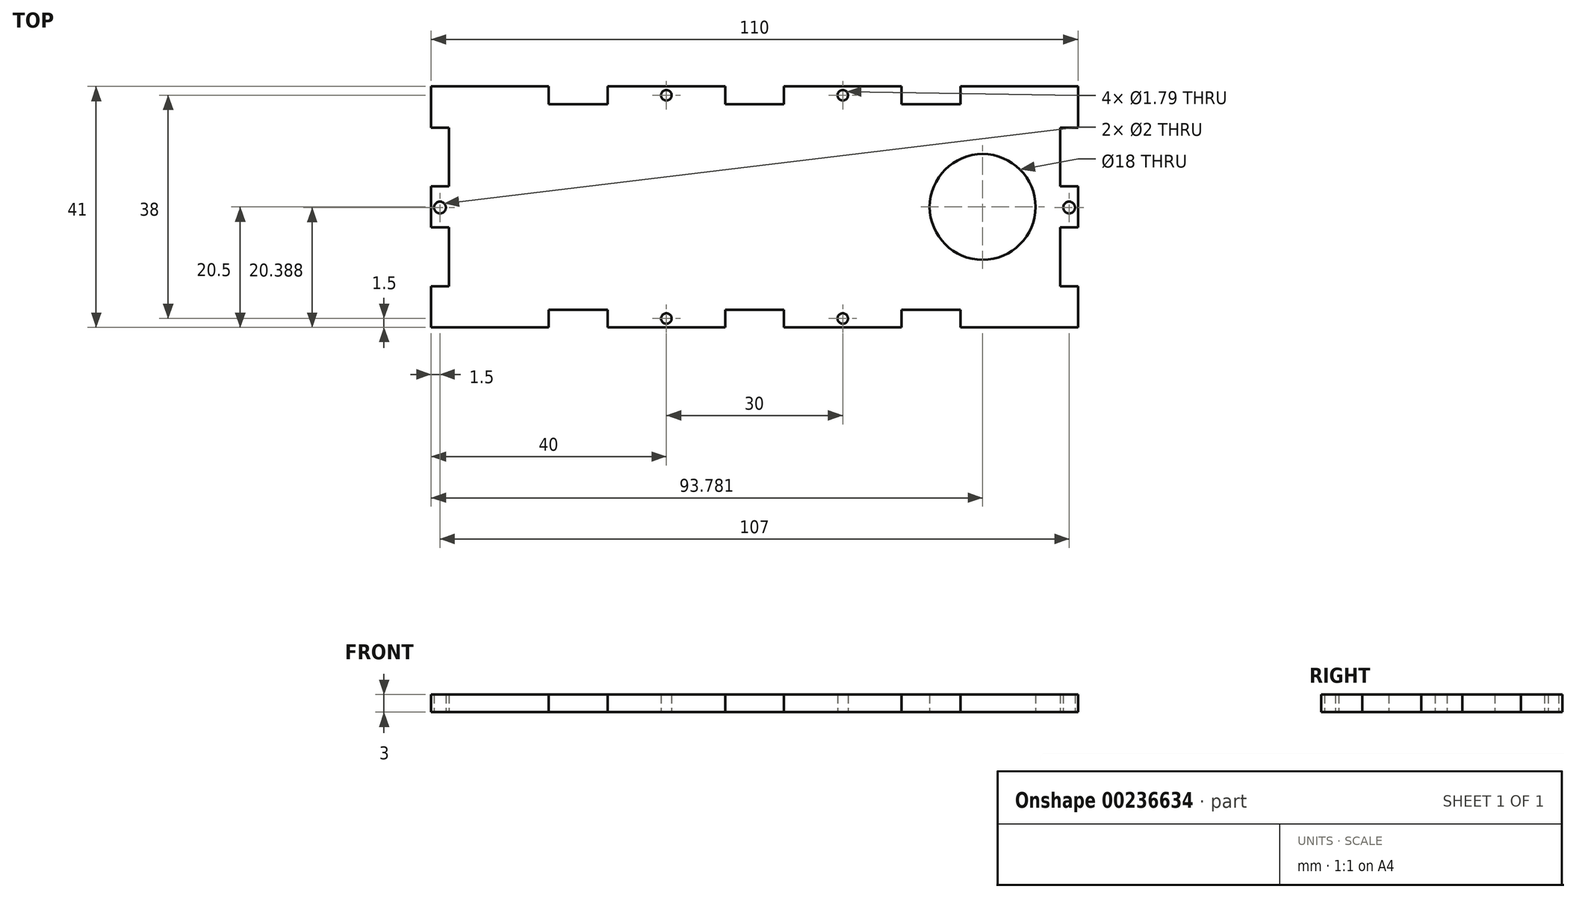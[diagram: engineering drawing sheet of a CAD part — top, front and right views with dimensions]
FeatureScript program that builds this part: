
annotation { "Feature Type Name" : "Feature", "Feature Type Description" : "" }
export const myFeature = defineFeature(function(context is Context, id is Id, definition is map)
    precondition{}
    {
        {
            var Q0;
            Q0=qCreatedBy(makeId("Top.planeOp"),FACE);
            var sketch = newSketch(context, id + "F0", { "sketchPlane" : qUnion([Q0])});
            skLineSegment(sketch, "E0", {"start": v(0, 0) * mm, "end": v(0, 7) * mm});
            skLineSegment(sketch, "E1", {"start": v(0, 7) * mm, "end": v(3, 7) * mm});
            skLineSegment(sketch, "E2", {"start": v(3, 7) * mm, "end": v(3, 17) * mm});
            skLineSegment(sketch, "E3", {"start": v(3, 17) * mm, "end": v(0, 17) * mm});
            skLineSegment(sketch, "E4", {"start": v(0, 17) * mm, "end": v(0, 24) * mm});
            skLineSegment(sketch, "E5", {"start": v(0, 24) * mm, "end": v(3, 24) * mm});
            skLineSegment(sketch, "E6", {"start": v(3, 24) * mm, "end": v(3, 34) * mm});
            skLineSegment(sketch, "E7", {"start": v(3, 34) * mm, "end": v(0, 34) * mm});
            skLineSegment(sketch, "E8", {"start": v(0, 34) * mm, "end": v(0, 41) * mm});
            skLineSegment(sketch, "E9", {"start": v(0, 41) * mm, "end": v(20, 41) * mm});
            skLineSegment(sketch, "E10", {"start": v(20, 41) * mm, "end": v(20, 38) * mm});
            skLineSegment(sketch, "E11", {"start": v(20, 38) * mm, "end": v(30, 38) * mm});
            skLineSegment(sketch, "E12", {"start": v(30, 38) * mm, "end": v(30, 41) * mm});
            skLineSegment(sketch, "E13", {"start": v(30, 41) * mm, "end": v(50, 41) * mm});
            skLineSegment(sketch, "E14", {"start": v(50, 41) * mm, "end": v(50, 38) * mm});
            skLineSegment(sketch, "E15", {"start": v(50, 38) * mm, "end": v(55, 38) * mm});
            skLineSegment(sketch, "E16", {"start": v(55, 41) * mm, "end": v(55, 0) * mm, "construction": true});
            skLineSegment(sketch, "E17", {"start": v(0, 20.5) * mm, "end": v(55, 20.5) * mm, "construction": true});
            skLineSegment(sketch, "E18.MirrorCS", {"start": v(20, 0) * mm, "end": v(20, 3) * mm});
            skLineSegment(sketch, "E19.MirrorCS", {"start": v(30, 3) * mm, "end": v(30, 0) * mm});
            skLineSegment(sketch, "E20.MirrorCS", {"start": v(50, 0) * mm, "end": v(50, 3) * mm});
            skLineSegment(sketch, "E21.MirrorCS", {"start": v(30, 0) * mm, "end": v(50, 0) * mm});
            skLineSegment(sketch, "E22.MirrorCS", {"start": v(20, 3) * mm, "end": v(30, 3) * mm});
            skLineSegment(sketch, "E23.MirrorCS", {"start": v(50, 3) * mm, "end": v(55, 3) * mm});
            skLineSegment(sketch, "E24.MirrorCS", {"start": v(0, 0) * mm, "end": v(20, 0) * mm});
            skLineSegment(sketch, "E25.MirrorCS", {"start": v(90, 41) * mm, "end": v(90, 38) * mm});
            skLineSegment(sketch, "E26.MirrorCS", {"start": v(80, 38) * mm, "end": v(80, 41) * mm});
            skLineSegment(sketch, "E27.MirrorCS", {"start": v(107, 34) * mm, "end": v(110, 34) * mm});
            skLineSegment(sketch, "E28.MirrorCS", {"start": v(110, 24) * mm, "end": v(107, 24) * mm});
            skLineSegment(sketch, "E29.MirrorCS", {"start": v(60, 41) * mm, "end": v(60, 38) * mm});
            skLineSegment(sketch, "E30.MirrorCS", {"start": v(80, 3) * mm, "end": v(80, 0) * mm});
            skLineSegment(sketch, "E31.MirrorCS", {"start": v(110, 7) * mm, "end": v(107, 7) * mm});
            skLineSegment(sketch, "E32.MirrorCS", {"start": v(90, 0) * mm, "end": v(90, 3) * mm});
            skLineSegment(sketch, "E33.MirrorCS", {"start": v(60, 0) * mm, "end": v(60, 3) * mm});
            skLineSegment(sketch, "E34.MirrorCS", {"start": v(107, 17) * mm, "end": v(110, 17) * mm});
            skLineSegment(sketch, "E35.MirrorCS", {"start": v(110, 17) * mm, "end": v(110, 24) * mm});
            skLineSegment(sketch, "E36.MirrorCS", {"start": v(60, 3) * mm, "end": v(55, 3) * mm});
            skLineSegment(sketch, "E37.MirrorCS", {"start": v(110, 41) * mm, "end": v(90, 41) * mm});
            skLineSegment(sketch, "E38.MirrorCS", {"start": v(80, 0) * mm, "end": v(60, 0) * mm});
            skLineSegment(sketch, "E39.MirrorCS", {"start": v(90, 38) * mm, "end": v(80, 38) * mm});
            skLineSegment(sketch, "E40.MirrorCS", {"start": v(80, 41) * mm, "end": v(60, 41) * mm});
            skLineSegment(sketch, "E41.MirrorCS", {"start": v(107, 24) * mm, "end": v(107, 34) * mm});
            skLineSegment(sketch, "E42.MirrorCS", {"start": v(110, 0) * mm, "end": v(90, 0) * mm});
            skLineSegment(sketch, "E43.MirrorCS", {"start": v(60, 38) * mm, "end": v(55, 38) * mm});
            skLineSegment(sketch, "E44.MirrorCS", {"start": v(107, 7) * mm, "end": v(107, 17) * mm});
            skLineSegment(sketch, "E45.MirrorCS", {"start": v(90, 3) * mm, "end": v(80, 3) * mm});
            skLineSegment(sketch, "E46.MirrorCS", {"start": v(110, 20.5) * mm, "end": v(55, 20.5) * mm, "construction": true});
            skLineSegment(sketch, "E47.MirrorCS", {"start": v(110, 34) * mm, "end": v(110, 41) * mm});
            skLineSegment(sketch, "E48.MirrorCS", {"start": v(110, 0) * mm, "end": v(110, 7) * mm});
            skCircle(sketch, "E49", {"center": v(1.5, 20.39) * mm, "radius": 1 * mm});
            skCircle(sketch, "E50", {"center": v(40, 39.5) * mm, "radius": 0.9 * mm});
            skCircle(sketch, "E51.MirrorC", {"center": v(40, 1.5) * mm, "radius": 0.9 * mm});
            skCircle(sketch, "E52.MirrorC", {"center": v(108.5, 20.39) * mm, "radius": 1 * mm});
            skLineSegment(sketch, "E53.MirrorCS", {"start": v(55, 0) * mm, "end": v(55, 41) * mm, "construction": true});
            skCircle(sketch, "E54.MirrorC", {"center": v(70, 39.5) * mm, "radius": 0.9 * mm});
            skCircle(sketch, "E55.MirrorC", {"center": v(70, 1.5) * mm, "radius": 0.9 * mm});
            skCircle(sketch, "E56", {"center": v(93.78, 20.5) * mm, "radius": 9 * mm});
            skSolve(sketch);
        }
        {
            var Q0;
            Q0=qSketchRegion(id+"F0",true);
            extrude(context, id + "F1", {"entities" : qUnion([Q0]), "depth" : 3 * mm});
        }
    });
